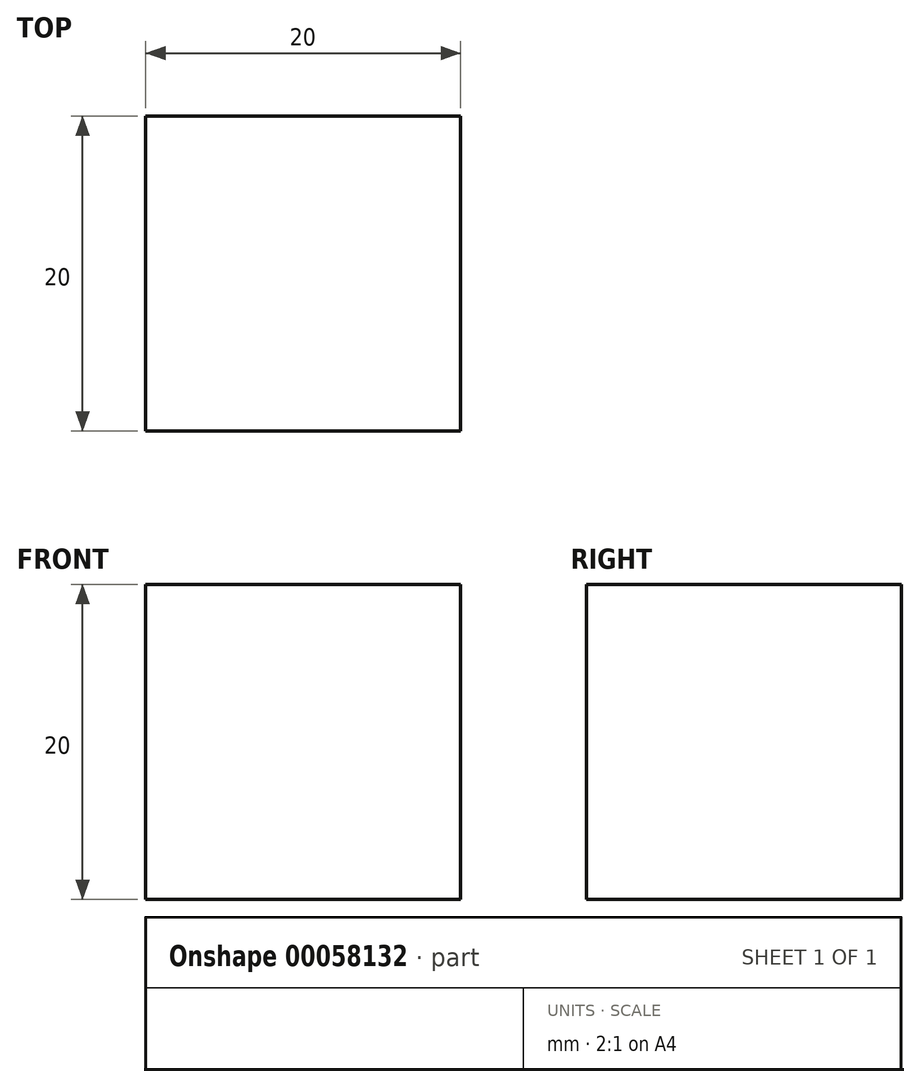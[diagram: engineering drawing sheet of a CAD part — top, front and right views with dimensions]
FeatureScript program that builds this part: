
annotation { "Feature Type Name" : "Feature", "Feature Type Description" : "" }
export const myFeature = defineFeature(function(context is Context, id is Id, definition is map)
    precondition{}
    {
        {
            var Q0;
            Q0=qCreatedBy(makeId("Top.planeOp"),FACE);
            var sketch = newSketch(context, id + "F0", { "sketchPlane" : qUnion([Q0])});
            skLineSegment(sketch, "E0.bottom", {"start": v(0, 0) * mm, "end": v(20, 0) * mm});
            skLineSegment(sketch, "E0.top", {"start": v(0, -20) * mm, "end": v(20, -20) * mm});
            skLineSegment(sketch, "E0.left", {"start": v(0, 0) * mm, "end": v(0, -20) * mm});
            skLineSegment(sketch, "E0.right", {"start": v(20, 0) * mm, "end": v(20, -20) * mm});
            skSolve(sketch);
        }
        {
            var Q0;
            Q0=makeQuery(id+"F0.imprint","IMPRINT",FACE,{"disambiguationData":[TD([[makeQuery(id+"F0.imprint","IMPRINT",EDGE,{"derivedFrom":sQuery(id+"F0.wireOp",EDGE,"E0.bottom")}),-1.0]])]});
            extrude(context, id + "F1", {"entities" : qUnion([Q0]), "oppositeDirection" : true, "depth" : 20 * mm});
        }
    });
